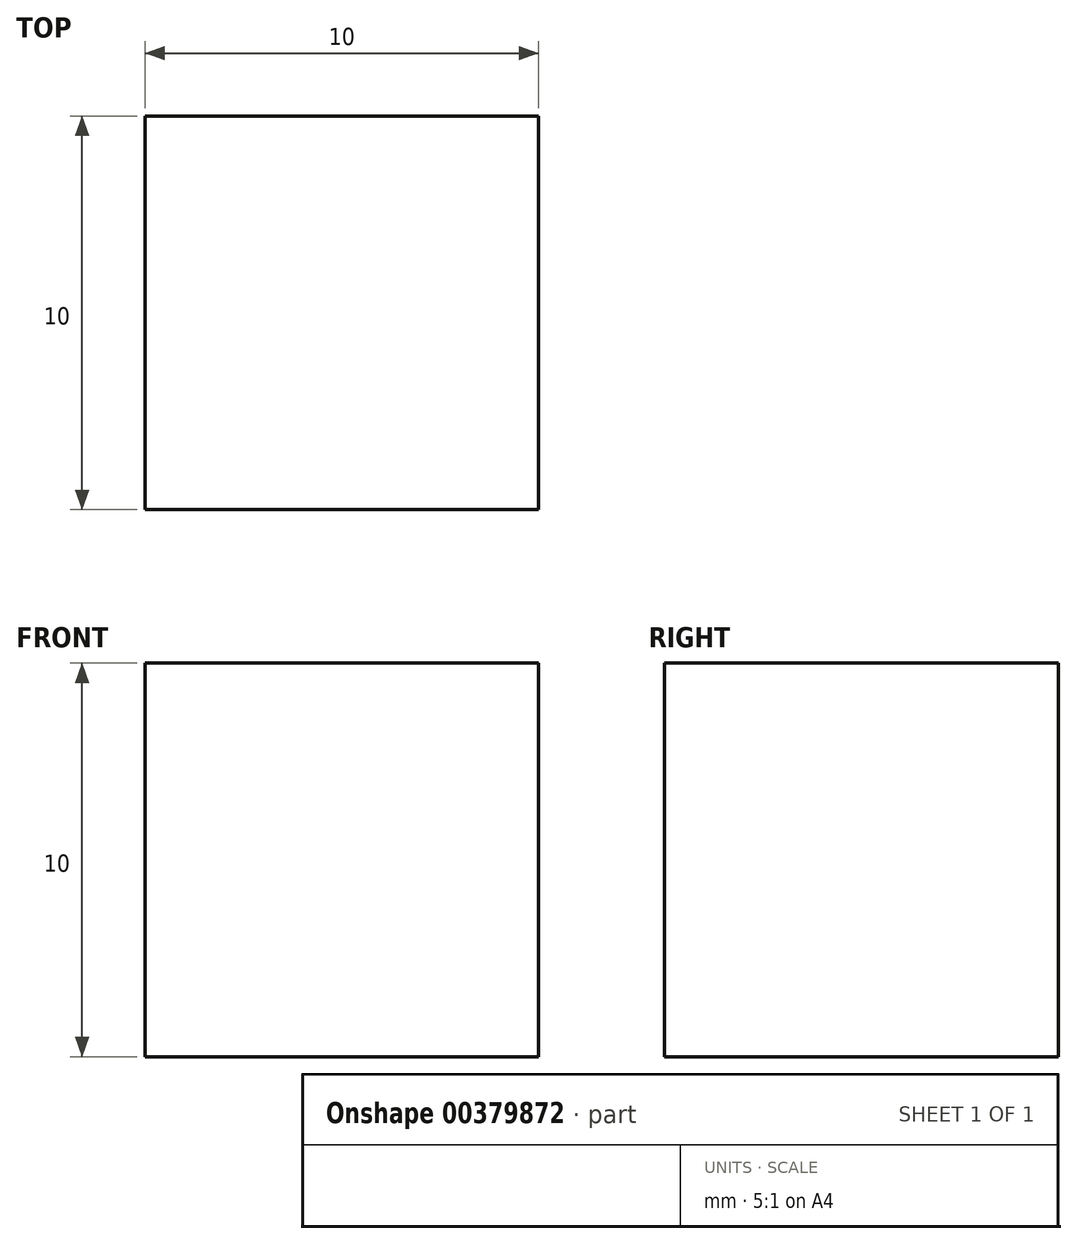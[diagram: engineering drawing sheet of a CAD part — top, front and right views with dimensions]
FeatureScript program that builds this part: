
annotation { "Feature Type Name" : "Feature", "Feature Type Description" : "" }
export const myFeature = defineFeature(function(context is Context, id is Id, definition is map)
    precondition{}
    {
        {
            var Q0;
            Q0=qCreatedBy(makeId("Top.planeOp"), FACE);
            var sketch = newSketch(context, id + "F0", { "sketchPlane" : qUnion([Q0])});
            skLineSegment(sketch, "E0.bottom", {"start": v(0, 0) * mm, "end": v(10, 0) * mm});
            skLineSegment(sketch, "E0.top", {"start": v(0, 10) * mm, "end": v(10, 10) * mm});
            skLineSegment(sketch, "E0.left", {"start": v(0, 0) * mm, "end": v(0, 10) * mm});
            skLineSegment(sketch, "E0.right", {"start": v(10, 0) * mm, "end": v(10, 10) * mm});
            skSolve(sketch);
        }
        {
            var Q0;
            Q0 = qSketchRegion(id + "F0", true);
            extrude(context, id + "F1", {"entities" : qUnion([Q0]), "depth" : 10 * mm, "offsetDistance" : 25 * mm});
        }
    });
